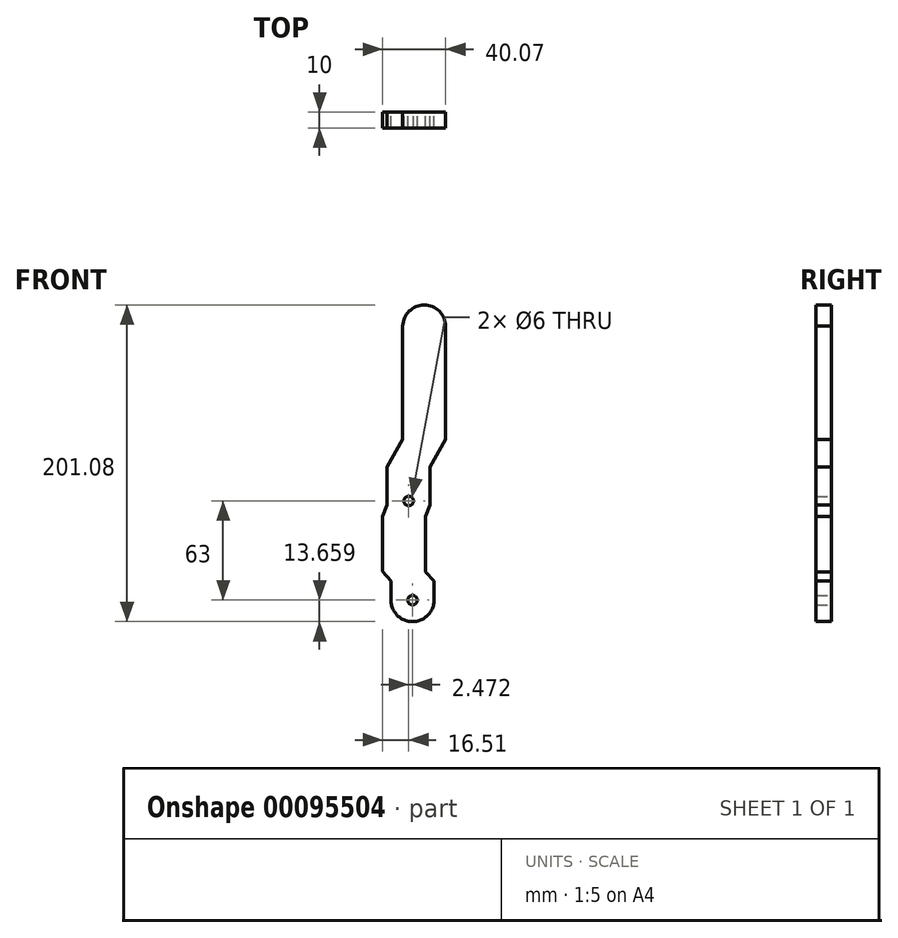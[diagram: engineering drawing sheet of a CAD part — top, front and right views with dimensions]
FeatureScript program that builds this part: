
annotation { "Feature Type Name" : "Feature", "Feature Type Description" : "" }
export const myFeature = defineFeature(function(context is Context, id is Id, definition is map)
    precondition{}
    {
        {
            var Q0;
            Q0=qCreatedBy(makeId("Front.planeOp"),FACE);
            var sketch = newSketch(context, id + "F0", { "sketchPlane" : qUnion([Q0])});
            skLineSegment(sketch, "E0", {"start": v(-48.71, 68.3) * mm, "end": v(-48.71, -3.7) * mm});
            skLineSegment(sketch, "E1", {"start": v(-48.71, -3.7) * mm, "end": v(-58.68, -21.23) * mm});
            skLineSegment(sketch, "E2", {"start": v(-58.68, -21.23) * mm, "end": v(-58.68, -45.23) * mm});
            skLineSegment(sketch, "E3", {"start": v(-58.68, -45.23) * mm, "end": v(-61.47, -52.73) * mm});
            skLineSegment(sketch, "E4", {"start": v(-61.47, -52.73) * mm, "end": v(-61.47, -87.73) * mm});
            skLineSegment(sketch, "E5", {"start": v(-61.47, -87.73) * mm, "end": v(-56.14, -93.7) * mm});
            skLineSegment(sketch, "E6", {"start": v(-56.14, -93.7) * mm, "end": v(-56.14, -105.75) * mm});
            skLineSegment(sketch, "E7", {"start": v(-21.4, 68.2) * mm, "end": v(-21.4, -3.8) * mm});
            skLineSegment(sketch, "E8", {"start": v(-21.4, -3.8) * mm, "end": v(-31.37, -21.32) * mm});
            skLineSegment(sketch, "E9", {"start": v(-31.37, -21.32) * mm, "end": v(-31.37, -45.32) * mm});
            skLineSegment(sketch, "E10", {"start": v(-31.37, -45.32) * mm, "end": v(-34.16, -52.81) * mm});
            skLineSegment(sketch, "E11", {"start": v(-34.16, -52.81) * mm, "end": v(-34.16, -87.81) * mm});
            skLineSegment(sketch, "E12", {"start": v(-34.16, -87.81) * mm, "end": v(-28.83, -93.78) * mm});
            skLineSegment(sketch, "E13", {"start": v(-28.83, -93.78) * mm, "end": v(-28.83, -105.83) * mm});
            skArc(sketch, "E14", {"start": v(-21.4, 67.66) * mm, "mid": v(-34.74, 81.59) * mm, "end": v(-48.71, 68.3) * mm});
            skCircle(sketch, "E15", {"center": v(-44.96, -42.83) * mm, "radius": 3 * mm});
            skCircle(sketch, "E16", {"center": v(-42.49, -105.83) * mm, "radius": 3 * mm});
            skArc(sketch, "E17", {"start": v(-56.14, -105.75) * mm, "mid": v(-42.53, -119.49) * mm, "end": v(-28.83, -105.83) * mm});
            skSolve(sketch);
        }
        {
            var Q0;
            {var subQ4=sQuery(id+"F0.wireOp",EDGE,"E0");Q0=makeQuery(id+"F0.imprint","IMPRINT",FACE,{"disambiguationData":[TD([[makeQuery(id+"F0.imprint","IMPRINT",EDGE,{"derivedFrom":subQ4}),1.0]])]});}
            extrude(context, id + "F1", {"entities" : qUnion([Q0]), "depth" : 10 * mm});
        }
    });
